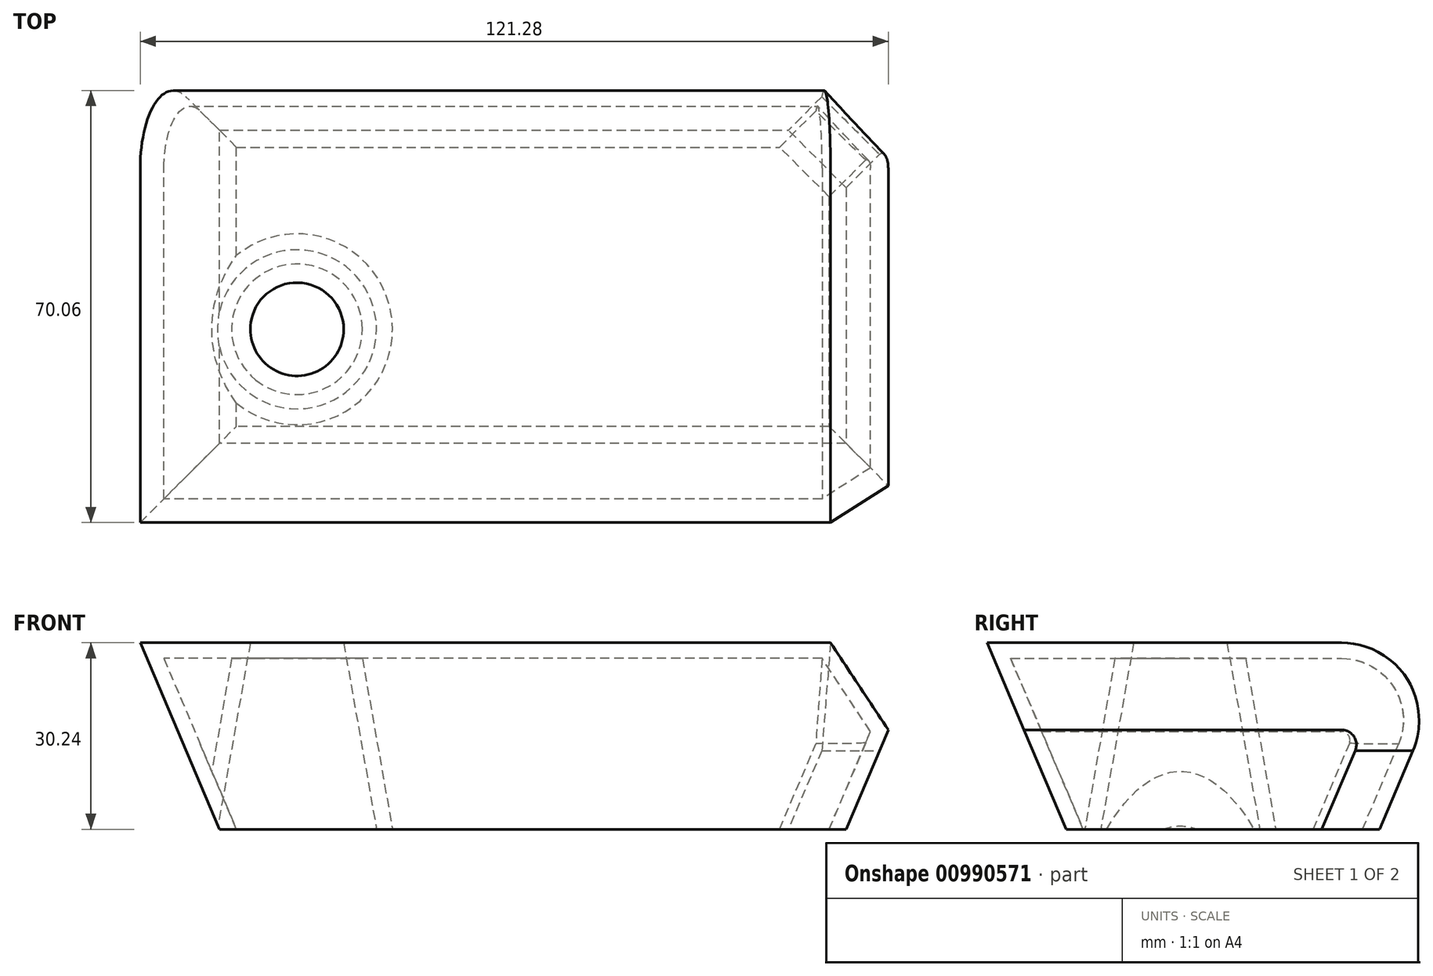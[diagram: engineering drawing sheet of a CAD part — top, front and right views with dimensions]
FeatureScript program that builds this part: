
annotation { "Feature Type Name" : "Feature", "Feature Type Description" : "" }
export const myFeature = defineFeature(function(context is Context, id is Id, definition is map)
    precondition{}
    {
        {
            var Q0;
            Q0=qCreatedBy(makeId("Top.planeOp"),FACE);
            var sketch = newSketch(context, id + "F0", { "sketchPlane" : qUnion([Q0])});
            skLineSegment(sketch, "E0.bottom", {"start": v(-54.55, 1.33) * mm, "end": v(47.05, 1.33) * mm});
            skLineSegment(sketch, "E0.top", {"start": v(-54.55, -49.47) * mm, "end": v(47.05, -49.47) * mm});
            skLineSegment(sketch, "E0.left", {"start": v(-54.55, 1.33) * mm, "end": v(-54.55, -49.47) * mm});
            skLineSegment(sketch, "E0.right", {"start": v(47.05, 1.33) * mm, "end": v(47.05, -49.47) * mm});
            skLineSegment(sketch, "E1.bottom", {"start": v(47.05, -17.25) * mm, "end": v(47.05, -17.25) * mm});
            skLineSegment(sketch, "E1.top", {"start": v(47.05, -49.47) * mm, "end": v(47.05, -49.47) * mm});
            skLineSegment(sketch, "E1.left", {"start": v(47.05, -17.25) * mm, "end": v(47.05, -49.47) * mm, "construction": true});
            skLineSegment(sketch, "E1.right", {"start": v(47.05, -17.25) * mm, "end": v(47.05, -49.47) * mm, "construction": true});
            skLineSegment(sketch, "E2.bottom", {"start": v(47.05, 1.33) * mm, "end": v(47.05, 1.33) * mm});
            skLineSegment(sketch, "E2.left", {"start": v(47.05, 1.33) * mm, "end": v(47.05, -49.47) * mm, "construction": true});
            skLineSegment(sketch, "E2.right", {"start": v(47.05, 1.33) * mm, "end": v(47.05, -49.47) * mm, "construction": true});
            skSolve(sketch);
        }
        {
            var Q0;
            Q0=makeQuery(id+"F0.imprint","IMPRINT",FACE,{"disambiguationData":[TD([[makeQuery(id+"F0.imprint","IMPRINT",EDGE,{"derivedFrom":sQuery(id+"F0.wireOp",EDGE,"E0.bottom")}),-1.0]])]});
            extrude(context, id + "F1", {"entities" : qUnion([Q0]), "depth" : 30.24 * mm, "offsetDistance" : 25.4 * mm, "hasDraft" : true, "draftAngle" : 23 * degree});
        }
        {
            var Q0;
            Q0=makeQuery(id+"F1.opExtrude","CAP_FACE",FACE,{"disambiguationData":[OSD([sQuery(id+"F0.wireOp",EDGE,"E0.bottom"),sQuery(id+"F0.wireOp",EDGE,"E0.top"),sQuery(id+"F0.wireOp",EDGE,"E0.left"),sQuery(id+"F0.wireOp",EDGE,"E0.right")])],"isStart":false});
            var sketch = newSketch(context, id + "F2", { "sketchPlane" : qUnion([Q0])});
            skCircle(sketch, "E3", {"center": v(-41.97, -30.97) * mm, "radius": 7.57 * mm});
            skSolve(sketch);
        }
        {
            var Q0;
            Q0 = qSketchRegion(id + "F2", true);
            extrude(context, id + "F3", {"entities" : qUnion([Q0]), "operationType" : NewBodyOperationType.REMOVE, "oppositeDirection" : true, "depth" : 48.52 * mm, "offsetDistance" : 25.4 * mm, "hasDraft" : true, "draftAngle" : 10 * degree});
        }
        {
            var Q0;
            Q0=makeQuery(id+"F1.opExtrude","CAP_EDGE",EDGE,{"disambiguationData":[OSD([sQuery(id+"F0.wireOp",EDGE,"E0.bottom")])],"isStart":false});
            fillet(context, id + "F4", {"entities" : qUnion([Q0]), "radius" : 12.57 * mm, "tangentPropagation" : true, "allowEdgeOverflow" : false});
        }
        {
            var Q0;
            Q0=makeQuery(id+"F4.opFillet","BLEND_EDGE",EDGE,{"blendedFrom":[makeQuery(id+"F1.opExtrude","CAP_EDGE",EDGE,{"disambiguationData":[OSD([sQuery(id+"F0.wireOp",EDGE,"E0.bottom")])],"isStart":false}),makeQuery(id+"F1.opExtrude","SWEPT_FACE",FACE,{"disambiguationData":[OSD([sQuery(id+"F0.wireOp",EDGE,"E0.right")])]})],"blendedInto":[makeQuery(id+"F1.opExtrude","SWEPT_FACE",FACE,{"disambiguationData":[OSD([sQuery(id+"F0.wireOp",EDGE,"E0.right")])]})]});
            chamfer(context, id + "F5", {"entities" : qUnion([Q0]), "width" : 10.16 * mm, "tangentPropagation" : true});
        }
        {
            var Q0;
            Q0=makeQuery(id+"F1.opExtrude","CAP_FACE",FACE,{"disambiguationData":[OSD([sQuery(id+"F0.wireOp",EDGE,"E0.bottom"),sQuery(id+"F0.wireOp",EDGE,"E0.top"),sQuery(id+"F0.wireOp",EDGE,"E0.left"),sQuery(id+"F0.wireOp",EDGE,"E0.right")])],"isStart":true});
            var Q1;
            Q1=makeQuery(id+"F1.opExtrude","SWEPT_BODY",BODY,{"disambiguationData":[OSD([sQuery(id+"F0.wireOp",EDGE,"E0.bottom"),sQuery(id+"F0.wireOp",EDGE,"E0.top"),sQuery(id+"F0.wireOp",EDGE,"E0.left"),sQuery(id+"F0.wireOp",EDGE,"E0.right")])]});
            shell(context, id + "F6", {"entities" : qUnion([Q0]), "parts" : qUnion([Q1]), "thickness" : 2.54 * mm});
        }
    });
